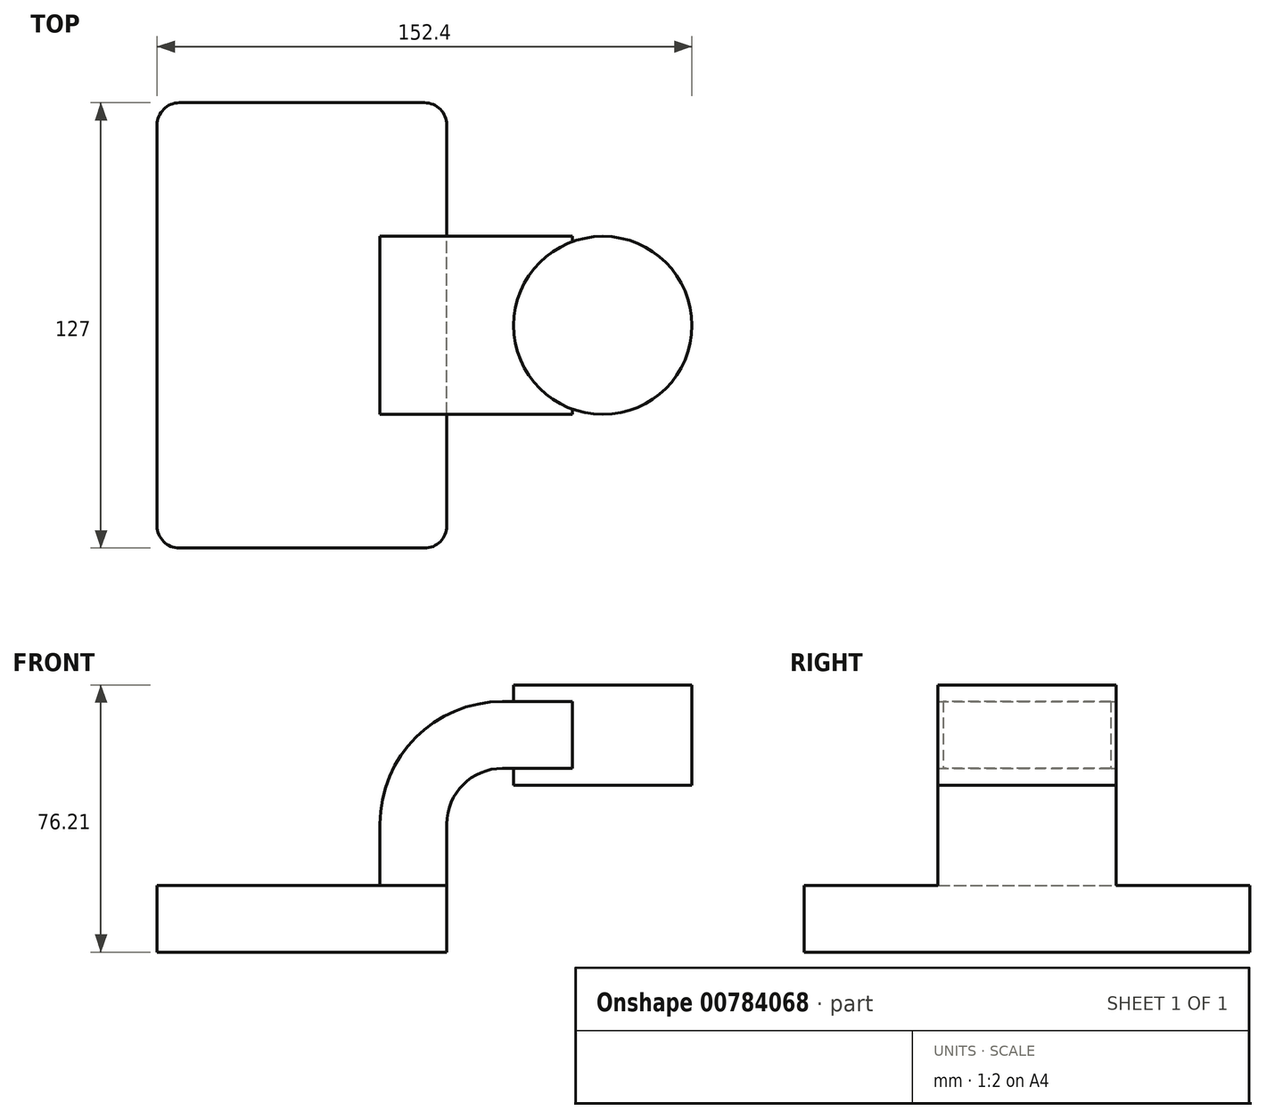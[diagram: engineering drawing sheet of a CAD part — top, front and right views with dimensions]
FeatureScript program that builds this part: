
annotation { "Feature Type Name" : "Feature", "Feature Type Description" : "" }
export const myFeature = defineFeature(function(context is Context, id is Id, definition is map)
    precondition{}
    {
        {
            var Q0;
            Q0=qCreatedBy(makeId("Front.planeOp"),FACE);
            var sketch = newSketch(context, id + "F0", { "sketchPlane" : qUnion([Q0])});
            skLineSegment(sketch, "E0.bottom", {"start": v(41.28, 9.53) * mm, "end": v(-41.28, 9.53) * mm});
            skLineSegment(sketch, "E0.top", {"start": v(41.28, -9.52) * mm, "end": v(-41.28, -9.52) * mm});
            skLineSegment(sketch, "E0.left", {"start": v(41.28, 9.53) * mm, "end": v(41.28, -9.52) * mm});
            skLineSegment(sketch, "E0.right", {"start": v(-41.28, 9.53) * mm, "end": v(-41.28, -9.52) * mm});
            skPoint(sketch, "E0.middle", {"position": v(0, 0) * mm});
            skLineSegment(sketch, "E1", {"start": v(41.28, 9.53) * mm, "end": v(41.28, 27) * mm});
            skArc(sketch, "E2", {"start": v(41.27, 27) * mm, "mid": v(45.92, 38.23) * mm, "end": v(57.15, 42.88) * mm});
            skLineSegment(sketch, "E3", {"start": v(57.15, 42.88) * mm, "end": v(77.06, 42.88) * mm});
            skLineSegment(sketch, "E4.bottom", {"start": v(111.13, 66.68) * mm, "end": v(60.33, 66.68) * mm});
            skLineSegment(sketch, "E4.top", {"start": v(111.13, 38.1) * mm, "end": v(60.33, 38.1) * mm});
            skLineSegment(sketch, "E4.left", {"start": v(111.13, 66.68) * mm, "end": v(111.13, 38.1) * mm});
            skLineSegment(sketch, "E4.right", {"start": v(60.33, 66.68) * mm, "end": v(60.33, 38.1) * mm});
            skPoint(sketch, "E4.middle", {"position": v(85.73, 52.39) * mm});
            skLineSegment(sketch, "E5.0", {"start": v(57.15, 61.93) * mm, "end": v(77.06, 61.93) * mm});
            skArc(sketch, "E5.1", {"start": v(22.23, 27) * mm, "mid": v(32.45, 51.7) * mm, "end": v(57.15, 61.93) * mm});
            skLineSegment(sketch, "E5.2", {"start": v(22.23, 9.53) * mm, "end": v(22.23, 27) * mm});
            skFitSpline(sketch, "E6", {"points": [v(-41.28, 9.53) * mm, v(57.15, 61.93) * mm], "startDerivative": vector(3.02, 84.72) * mm, "endDerivative": vector(171.45, -3.89) * mm});
            skLineSegment(sketch, "E7", {"start": v(77.06, 61.93) * mm, "end": v(77.06, 42.88) * mm});
            skLineSegment(sketch, "E8", {"start": v(85.73, 38.1) * mm, "end": v(85.73, 66.68) * mm});
            skSolve(sketch);
        }
        {
            var Q0;
            Q0=makeQuery(id+"F0.imprint","IMPRINT",FACE,{"disambiguationData":[TD([[makeQuery(id+"F0.imprint","IMPRINT",EDGE,{"derivedFrom":sQuery(id+"F0.wireOp",EDGE,"E0.top")}),-1.0]])]});
            extrude(context, id + "F1", {"entities" : qUnion([Q0]), "endBound" : BoundingType.SYMMETRIC, "depth" : 127 * mm, "offsetDistance" : 25.4 * mm});
        }
        {
            var Q0;
            {var subQ6=sQuery(id+"F0.wireOp",EDGE,"E1");Q0=makeQuery(id+"F0.imprint","IMPRINT",FACE,{"disambiguationData":[TD([[makeQuery(id+"F0.imprint","IMPRINT",EDGE,{"derivedFrom":subQ6}),1.0]])]});}
            var Q1;
            {var subQ0=sQuery(id+"F0.wireOp",EDGE,"E7");Q1=makeQuery(id+"F0.imprint","IMPRINT",FACE,{"disambiguationData":[TD([[makeQuery(id+"F0.imprint","IMPRINT",EDGE,{"derivedFrom":subQ0}),-1.0]])]});}
            extrude(context, id + "F2", {"entities" : qUnion([Q0, Q1]), "operationType" : NewBodyOperationType.ADD, "endBound" : BoundingType.SYMMETRIC, "depth" : 50.8 * mm, "offsetDistance" : 25.4 * mm});
        }
        {
            var Q0;
            Q0=makeQuery(id+"F0.imprint","IMPRINT",FACE,{"disambiguationData":[TD([[makeQuery(id+"F0.imprint","IMPRINT",EDGE,{"derivedFrom":sQuery(id+"F0.wireOp",EDGE,"E5.1")}),1.0]])]});
            extrude(context, id + "F3", {"entities" : qUnion([Q0]), "operationType" : NewBodyOperationType.ADD, "endBound" : BoundingType.SYMMETRIC, "depth" : 16.56 * mm, "offsetDistance" : 25.4 * mm});
        }
        {
            var Q0;
            {var subQ0=sQuery(id+"F0.wireOp",EDGE,"E4.left");Q0=makeQuery(id+"F0.imprint","IMPRINT",FACE,{"disambiguationData":[TD([[makeQuery(id+"F0.imprint","IMPRINT",EDGE,{"derivedFrom":subQ0}),-1.0]])]});}
            var Q1;
            Q1=sQuery(id+"F0.wireOp",EDGE,"E8");
            revolve(context, id + "F4", {"operationType" : NewBodyOperationType.ADD, "surfaceOperationType" : NewSurfaceOperationType.NEW, "entities" : qUnion([Q0]), "axis" : qUnion([Q1]), "revolveType" : RevolveType.FULL});
        }
        {
            var Q0;
            Q0=makeQuery(id+"F1.opExtrude","CAP_EDGE",EDGE,{"disambiguationData":[OSD([sQuery(id+"F0.wireOp",EDGE,"E0.left")])],"isStart":false});
            var Q1;
            Q1=makeQuery(id+"F1.opExtrude","CAP_EDGE",EDGE,{"disambiguationData":[OSD([sQuery(id+"F0.wireOp",EDGE,"E0.right")])],"isStart":false});
            var Q2;
            Q2=makeQuery(id+"F1.opExtrude","CAP_EDGE",EDGE,{"disambiguationData":[OSD([sQuery(id+"F0.wireOp",EDGE,"E0.left")])],"isStart":true});
            var Q3;
            Q3=makeQuery(id+"F1.opExtrude","CAP_EDGE",EDGE,{"disambiguationData":[OSD([sQuery(id+"F0.wireOp",EDGE,"E0.right")])],"isStart":true});
            fillet(context, id + "F5", {"entities" : qUnion([Q0, Q1, Q2, Q3]), "radius" : 6.35 * mm, "tangentPropagation" : true, "allowEdgeOverflow" : false});
        }
    });
